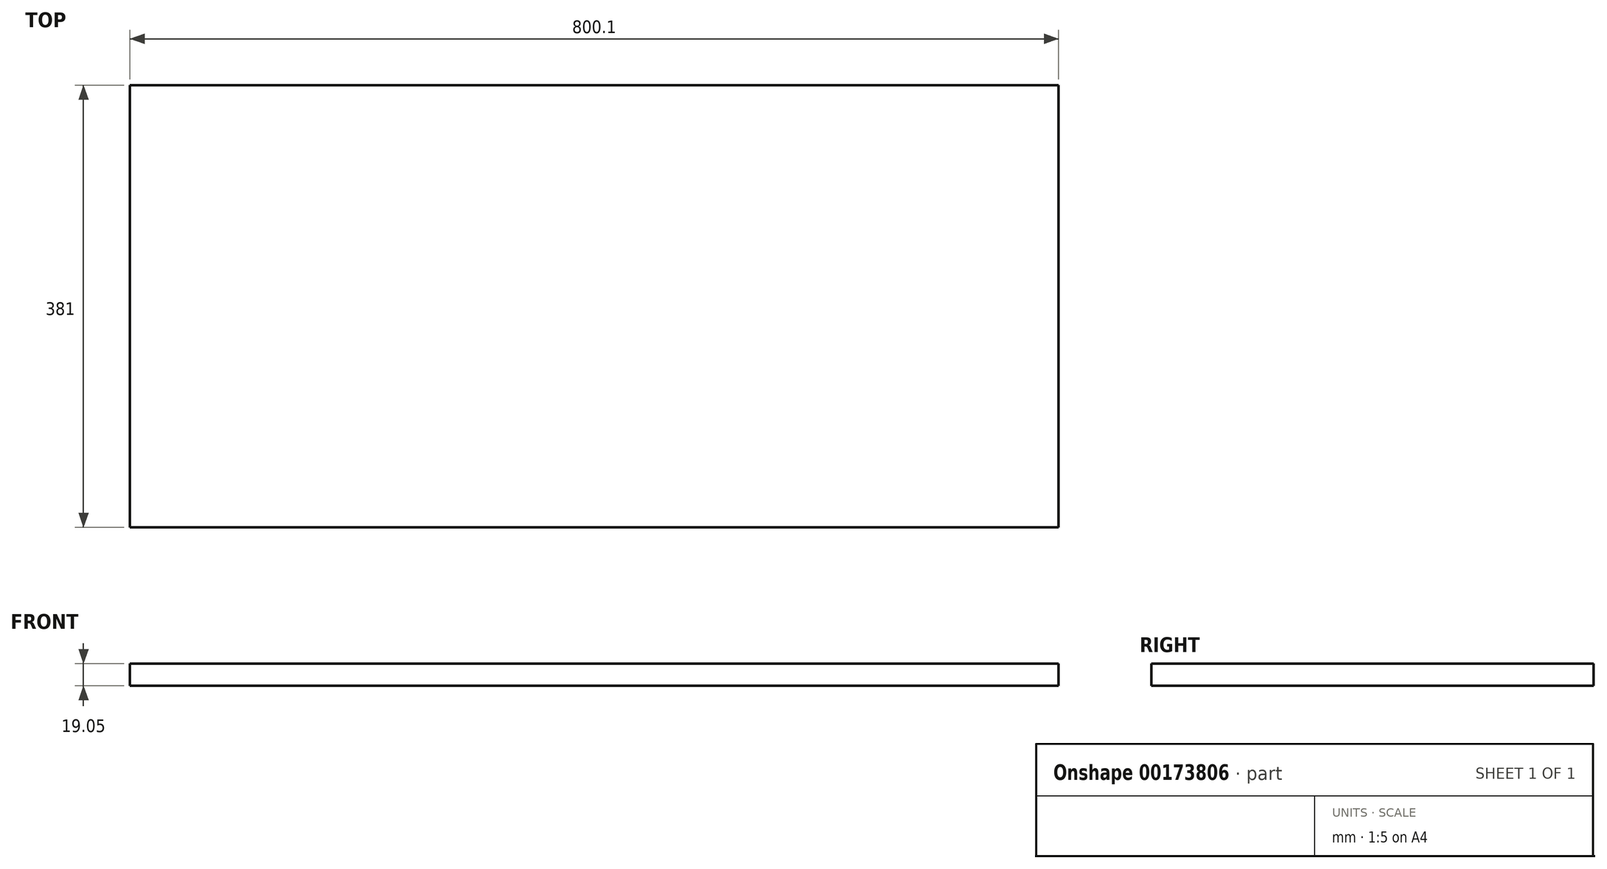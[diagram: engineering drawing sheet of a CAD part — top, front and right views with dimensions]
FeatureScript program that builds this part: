
annotation { "Feature Type Name" : "Feature", "Feature Type Description" : "" }
export const myFeature = defineFeature(function(context is Context, id is Id, definition is map)
    precondition{}
    {
        {
            var Q0;
            Q0=qCreatedBy(makeId("Top.planeOp"),FACE);
            var sketch = newSketch(context, id + "F0", { "sketchPlane" : qUnion([Q0])});
            skLineSegment(sketch, "E0.bottom", {"start": v(400.05, 190.5) * mm, "end": v(-400.05, 190.5) * mm});
            skLineSegment(sketch, "E0.top", {"start": v(400.05, -190.5) * mm, "end": v(-400.05, -190.5) * mm});
            skLineSegment(sketch, "E0.left", {"start": v(400.05, 190.5) * mm, "end": v(400.05, -190.5) * mm});
            skLineSegment(sketch, "E0.right", {"start": v(-400.05, 190.5) * mm, "end": v(-400.05, -190.5) * mm});
            skPoint(sketch, "E0.middle", {"position": v(0, 0) * mm});
            skSolve(sketch);
        }
        {
            var Q0;
            Q0 = qSketchRegion(id + "F0", true);
            extrude(context, id + "F1", {"entities" : qUnion([Q0]), "depth" : 19.05 * mm});
        }
    });
